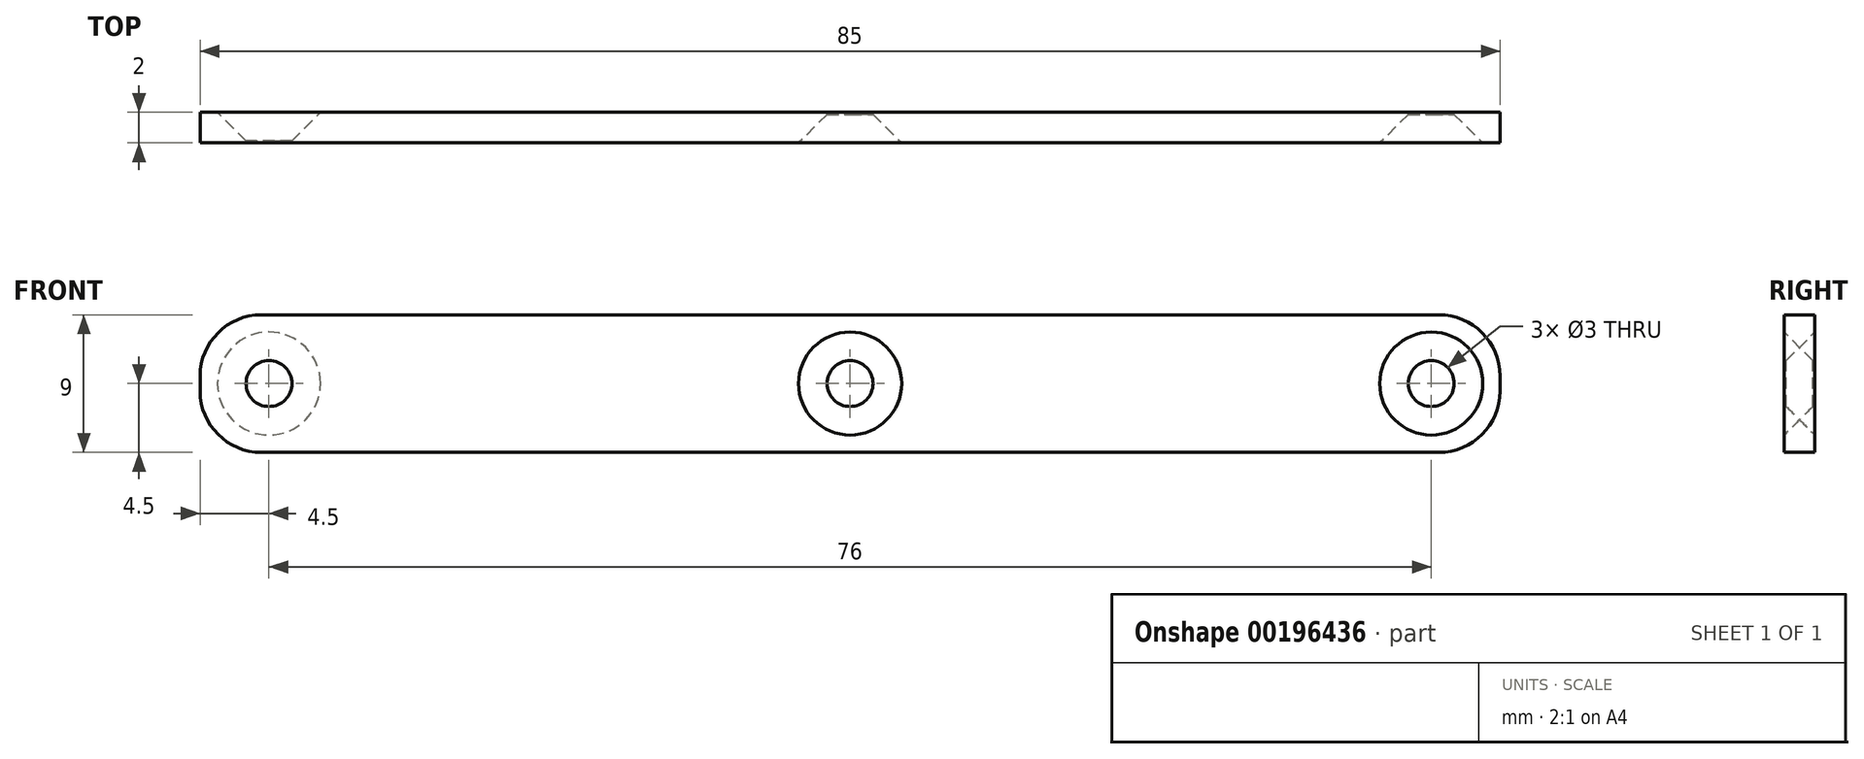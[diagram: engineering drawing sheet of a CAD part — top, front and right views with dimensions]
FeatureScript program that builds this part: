
annotation { "Feature Type Name" : "Feature", "Feature Type Description" : "" }
export const myFeature = defineFeature(function(context is Context, id is Id, definition is map)
    precondition{}
    {
        {
            var Q0;
            Q0=qCreatedBy(makeId("Front.planeOp"),FACE);
            var sketch = newSketch(context, id + "F0", { "sketchPlane" : qUnion([Q0])});
            skLineSegment(sketch, "E0.bottom", {"start": v(42.5, 4.5) * mm, "end": v(-42.5, 4.5) * mm});
            skLineSegment(sketch, "E0.top", {"start": v(42.5, -4.5) * mm, "end": v(-42.5, -4.5) * mm});
            skLineSegment(sketch, "E0.left", {"start": v(42.5, 4.5) * mm, "end": v(42.5, -4.5) * mm});
            skLineSegment(sketch, "E0.right", {"start": v(-42.5, 4.5) * mm, "end": v(-42.5, -4.5) * mm});
            skPoint(sketch, "E0.middle", {"position": v(0, 0) * mm});
            skCircle(sketch, "E1", {"center": v(0, 0) * mm, "radius": 1.5 * mm});
            skCircle(sketch, "E2", {"center": v(38, 0) * mm, "radius": 1.5 * mm});
            skCircle(sketch, "E3", {"center": v(-38, 0) * mm, "radius": 1.5 * mm});
            skSolve(sketch);
        }
        {
            var Q0;
            Q0=qSketchRegion(id+"F0",true);
            extrude(context, id + "F1", {"entities" : qUnion([Q0]), "depth" : 2 * mm});
        }
        {
            var Q0;
            Q0=makeQuery(id+"F1.opExtrude","SWEPT_EDGE",EDGE,{"disambiguationData":[OSD([sQuery(id+"F0.wireOp",EDGE,"E0.bottom"),sQuery(id+"F0.wireOp",EDGE,"E0.right")])]});
            var Q1;
            Q1=makeQuery(id+"F1.opExtrude","SWEPT_EDGE",EDGE,{"disambiguationData":[OSD([sQuery(id+"F0.wireOp",EDGE,"E0.top"),sQuery(id+"F0.wireOp",EDGE,"E0.right")])]});
            var Q2;
            Q2=makeQuery(id+"F1.opExtrude","SWEPT_EDGE",EDGE,{"disambiguationData":[OSD([sQuery(id+"F0.wireOp",EDGE,"E0.top"),sQuery(id+"F0.wireOp",EDGE,"E0.left")])]});
            var Q3;
            Q3=makeQuery(id+"F1.opExtrude","SWEPT_EDGE",EDGE,{"disambiguationData":[OSD([sQuery(id+"F0.wireOp",EDGE,"E0.bottom"),sQuery(id+"F0.wireOp",EDGE,"E0.left")])]});
            fillet(context, id + "F2", {"entities" : qUnion([Q0, Q1, Q2, Q3]), "radius" : 4 * mm, "tangentPropagation" : true, "allowEdgeOverflow" : false});
        }
        {
            var Q0;
            Q0=makeQuery(id+"F1.opExtrude","CAP_EDGE",EDGE,{"disambiguationData":[OSD([sQuery(id+"F0.wireOp",EDGE,"E2")])],"isStart":false});
            var Q1;
            Q1=makeQuery(id+"F1.opExtrude","CAP_EDGE",EDGE,{"disambiguationData":[OSD([sQuery(id+"F0.wireOp",EDGE,"E1")])],"isStart":false});
            var Q2;
            Q2=makeQuery(id+"F1.opExtrude","CAP_EDGE",EDGE,{"disambiguationData":[OSD([sQuery(id+"F0.wireOp",EDGE,"E3")])],"isStart":true});
            chamfer(context, id + "F3", {"entities" : qUnion([Q0, Q1, Q2]), "width" : 1.87 * mm, "tangentPropagation" : true});
        }
    });
